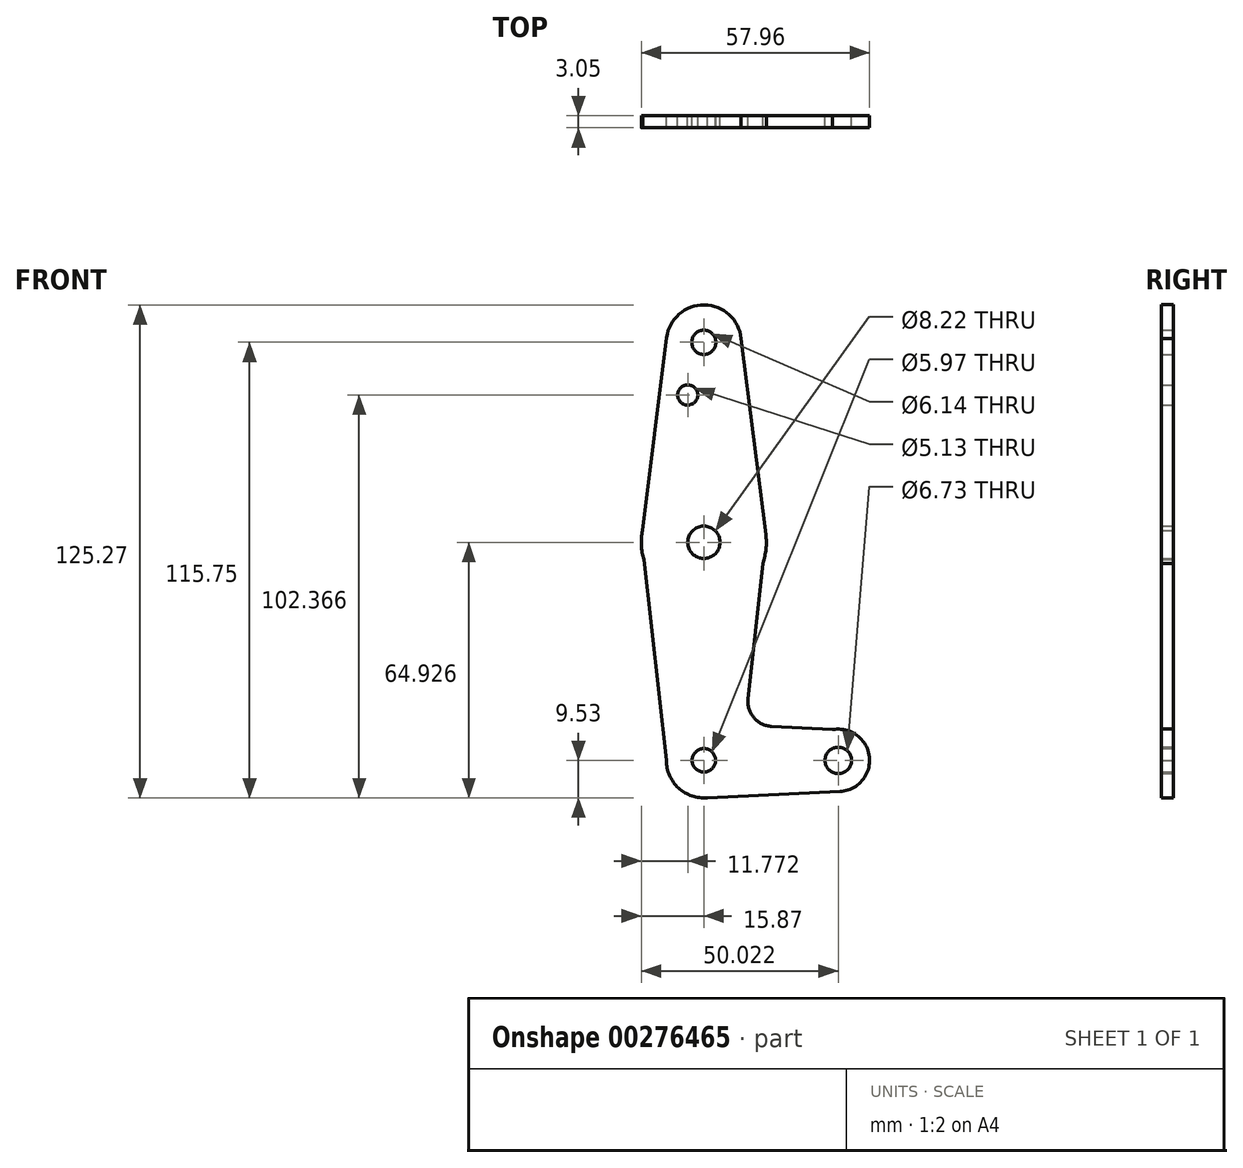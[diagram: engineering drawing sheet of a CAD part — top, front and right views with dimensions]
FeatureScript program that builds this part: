
annotation { "Feature Type Name" : "Feature", "Feature Type Description" : "" }
export const myFeature = defineFeature(function(context is Context, id is Id, definition is map)
    precondition{}
    {
        {
            var Q0;
            Q0=qCreatedBy(makeId("Front.planeOp"),FACE);
            var sketch = newSketch(context, id + "F0", { "sketchPlane" : qUnion([Q0])});
            skCircle(sketch, "E0", {"center": v(0, 0) * mm, "radius": 9.53 * mm});
            skCircle(sketch, "E1", {"center": v(0, 55.4) * mm, "radius": 15.88 * mm});
            skCircle(sketch, "E2", {"center": v(0, 106.22) * mm, "radius": 9.53 * mm});
            skCircle(sketch, "E3", {"center": v(34.15, 0) * mm, "radius": 7.94 * mm});
            skLineSegment(sketch, "E4", {"start": v(0, 106.22) * mm, "end": v(0, 55.4) * mm, "construction": true});
            skLineSegment(sketch, "E5", {"start": v(0, 55.4) * mm, "end": v(0, 0) * mm, "construction": true});
            skLineSegment(sketch, "E6", {"start": v(34.15, 0) * mm, "end": v(0, 0) * mm, "construction": true});
            skLineSegment(sketch, "E7", {"start": v(9.41, 107.67) * mm, "end": v(15.75, 57.38) * mm});
            skLineSegment(sketch, "E8", {"start": v(15.75, 57.38) * mm, "end": v(11.22, 15.65) * mm});
            skLineSegment(sketch, "E9", {"start": v(9.53, 0) * mm, "end": v(34.15, 0) * mm});
            skLineSegment(sketch, "E10", {"start": v(-9.52, 0) * mm, "end": v(-15.85, 56.31) * mm});
            skLineSegment(sketch, "E11", {"start": v(-15.59, 58.4) * mm, "end": v(-9.45, 107.4) * mm});
            skLineSegment(sketch, "E12", {"start": v(17.2, 8.62) * mm, "end": v(36.4, 7.61) * mm});
            skLineSegment(sketch, "E13", {"start": v(0, -9.53) * mm, "end": v(34.52, -7.93) * mm});
            skCircle(sketch, "E14", {"center": v(0, 106.22) * mm, "radius": 3.07 * mm});
            skCircle(sketch, "E15", {"center": v(0, 55.4) * mm, "radius": 4.1 * mm});
            skCircle(sketch, "E16", {"center": v(0, 0) * mm, "radius": 2.99 * mm});
            skCircle(sketch, "E17", {"center": v(34.15, 0) * mm, "radius": 3.36 * mm});
            skCircle(sketch, "E18", {"center": v(-4.1, 92.84) * mm, "radius": 2.56 * mm});
            skPoint(sketch, "E19.newPointB", {"position": v(0, 9.53) * mm});
            skArc(sketch, "E19.filletArc", {"start": v(11.22, 15.65) * mm, "mid": v(12.7, 10.85) * mm, "end": v(17.2, 8.62) * mm});
            skSolve(sketch);
        }
        {
            var Q0;
            Q0 = qSketchRegion(id + "F0", true);
            extrude(context, id + "F1", {"entities" : qUnion([Q0]), "depth" : 3.05 * mm});
        }
    });
